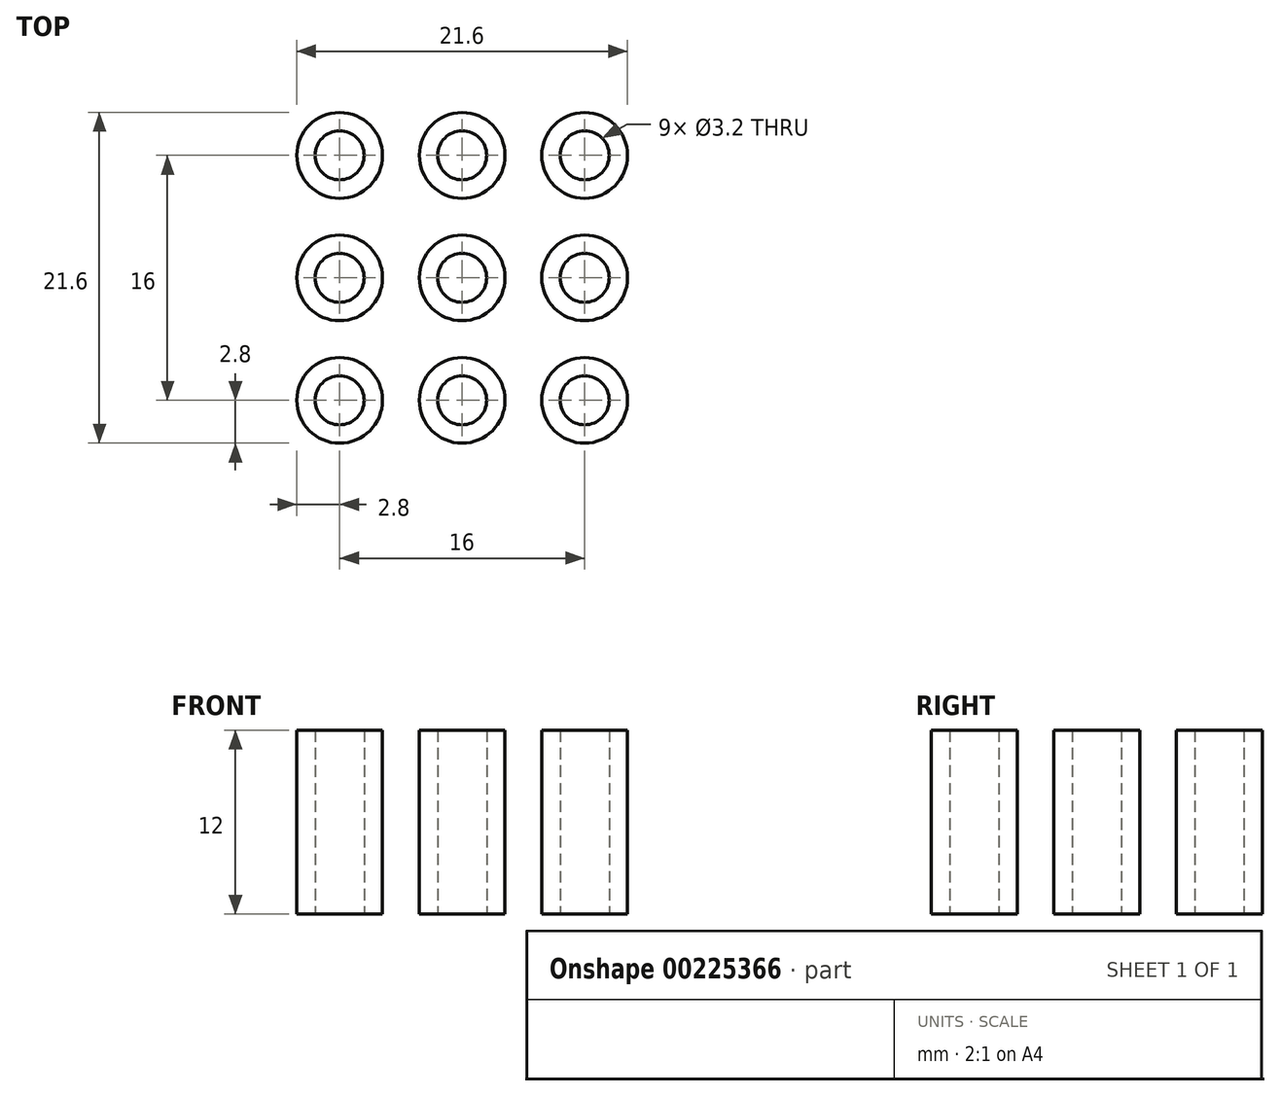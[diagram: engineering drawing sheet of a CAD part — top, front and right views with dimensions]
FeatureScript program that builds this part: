
annotation { "Feature Type Name" : "Feature", "Feature Type Description" : "" }
export const myFeature = defineFeature(function(context is Context, id is Id, definition is map)
    precondition{}
    {
        {
            var Q0;
            Q0=qCreatedBy(makeId("Top.planeOp"),FACE);
            var sketch = newSketch(context, id + "F0", { "sketchPlane" : qUnion([Q0])});
            skCircle(sketch, "E0", {"center": v(0, 0) * mm, "radius": 1.6 * mm});
            skCircle(sketch, "E1", {"center": v(0, 0) * mm, "radius": 2.8 * mm});
            skCircle(sketch, "E2.0.1.0", {"center": v(0, 8) * mm, "radius": 2.8 * mm});
            skCircle(sketch, "E2.0.1.1", {"center": v(0, 8) * mm, "radius": 1.6 * mm});
            skCircle(sketch, "E2.0.2.0", {"center": v(0, 16) * mm, "radius": 2.8 * mm});
            skCircle(sketch, "E2.0.2.1", {"center": v(0, 16) * mm, "radius": 1.6 * mm});
            skCircle(sketch, "E2.1.0.0", {"center": v(8, 0) * mm, "radius": 2.8 * mm});
            skCircle(sketch, "E2.1.0.1", {"center": v(8, 0) * mm, "radius": 1.6 * mm});
            skCircle(sketch, "E2.1.1.0", {"center": v(8, 8) * mm, "radius": 2.8 * mm});
            skCircle(sketch, "E2.1.1.1", {"center": v(8, 8) * mm, "radius": 1.6 * mm});
            skCircle(sketch, "E2.1.2.0", {"center": v(8, 16) * mm, "radius": 2.8 * mm});
            skCircle(sketch, "E2.1.2.1", {"center": v(8, 16) * mm, "radius": 1.6 * mm});
            skCircle(sketch, "E2.2.0.0", {"center": v(16, 0) * mm, "radius": 2.8 * mm});
            skCircle(sketch, "E2.2.0.1", {"center": v(16, 0) * mm, "radius": 1.6 * mm});
            skCircle(sketch, "E2.2.1.0", {"center": v(16, 8) * mm, "radius": 2.8 * mm});
            skCircle(sketch, "E2.2.1.1", {"center": v(16, 8) * mm, "radius": 1.6 * mm});
            skCircle(sketch, "E2.2.2.0", {"center": v(16, 16) * mm, "radius": 2.8 * mm});
            skCircle(sketch, "E2.2.2.1", {"center": v(16, 16) * mm, "radius": 1.6 * mm});
            skLineSegment(sketch, "E2.direction1", {"start": v(0, 0) * mm, "end": v(8, 0) * mm, "construction": true});
            skLineSegment(sketch, "E2.direction2", {"start": v(0, 0) * mm, "end": v(0, 8) * mm, "construction": true});
            skSolve(sketch);
        }
        {
            var Q0;
            Q0=makeQuery(id+"F0.imprint","IMPRINT",FACE,{"disambiguationData":[TD([[makeQuery(id+"F0.imprint","IMPRINT",EDGE,{"derivedFrom":sQuery(id+"F0.wireOp",EDGE,"E2.0.2.0")}),1.0]])]});
            var Q1;
            Q1=makeQuery(id+"F0.imprint","IMPRINT",FACE,{"disambiguationData":[TD([[makeQuery(id+"F0.imprint","IMPRINT",EDGE,{"derivedFrom":sQuery(id+"F0.wireOp",EDGE,"E2.1.2.0")}),1.0]])]});
            var Q2;
            Q2=makeQuery(id+"F0.imprint","IMPRINT",FACE,{"disambiguationData":[TD([[makeQuery(id+"F0.imprint","IMPRINT",EDGE,{"derivedFrom":sQuery(id+"F0.wireOp",EDGE,"E2.2.2.0")}),1.0]])]});
            var Q3;
            Q3=makeQuery(id+"F0.imprint","IMPRINT",FACE,{"disambiguationData":[TD([[makeQuery(id+"F0.imprint","IMPRINT",EDGE,{"derivedFrom":sQuery(id+"F0.wireOp",EDGE,"E2.2.1.0")}),1.0]])]});
            var Q4;
            Q4=makeQuery(id+"F0.imprint","IMPRINT",FACE,{"disambiguationData":[TD([[makeQuery(id+"F0.imprint","IMPRINT",EDGE,{"derivedFrom":sQuery(id+"F0.wireOp",EDGE,"E2.2.0.0")}),1.0]])]});
            var Q5;
            Q5=makeQuery(id+"F0.imprint","IMPRINT",FACE,{"disambiguationData":[TD([[makeQuery(id+"F0.imprint","IMPRINT",EDGE,{"derivedFrom":sQuery(id+"F0.wireOp",EDGE,"E2.1.0.0")}),1.0]])]});
            var Q6;
            Q6=makeQuery(id+"F0.imprint","IMPRINT",FACE,{"disambiguationData":[TD([[makeQuery(id+"F0.imprint","IMPRINT",EDGE,{"derivedFrom":sQuery(id+"F0.wireOp",EDGE,"E2.1.1.0")}),1.0]])]});
            var Q7;
            Q7=makeQuery(id+"F0.imprint","IMPRINT",FACE,{"disambiguationData":[TD([[makeQuery(id+"F0.imprint","IMPRINT",EDGE,{"derivedFrom":sQuery(id+"F0.wireOp",EDGE,"E2.0.1.0")}),1.0]])]});
            var Q8;
            Q8=makeQuery(id+"F0.imprint","IMPRINT",FACE,{"disambiguationData":[TD([[makeQuery(id+"F0.imprint","IMPRINT",EDGE,{"derivedFrom":sQuery(id+"F0.wireOp",EDGE,"E0")}),-1.0]])]});
            extrude(context, id + "F1", {"entities" : qUnion([Q0, Q1, Q2, Q3, Q4, Q5, Q6, Q7, Q8]), "depth" : 12 * mm});
        }
    });
